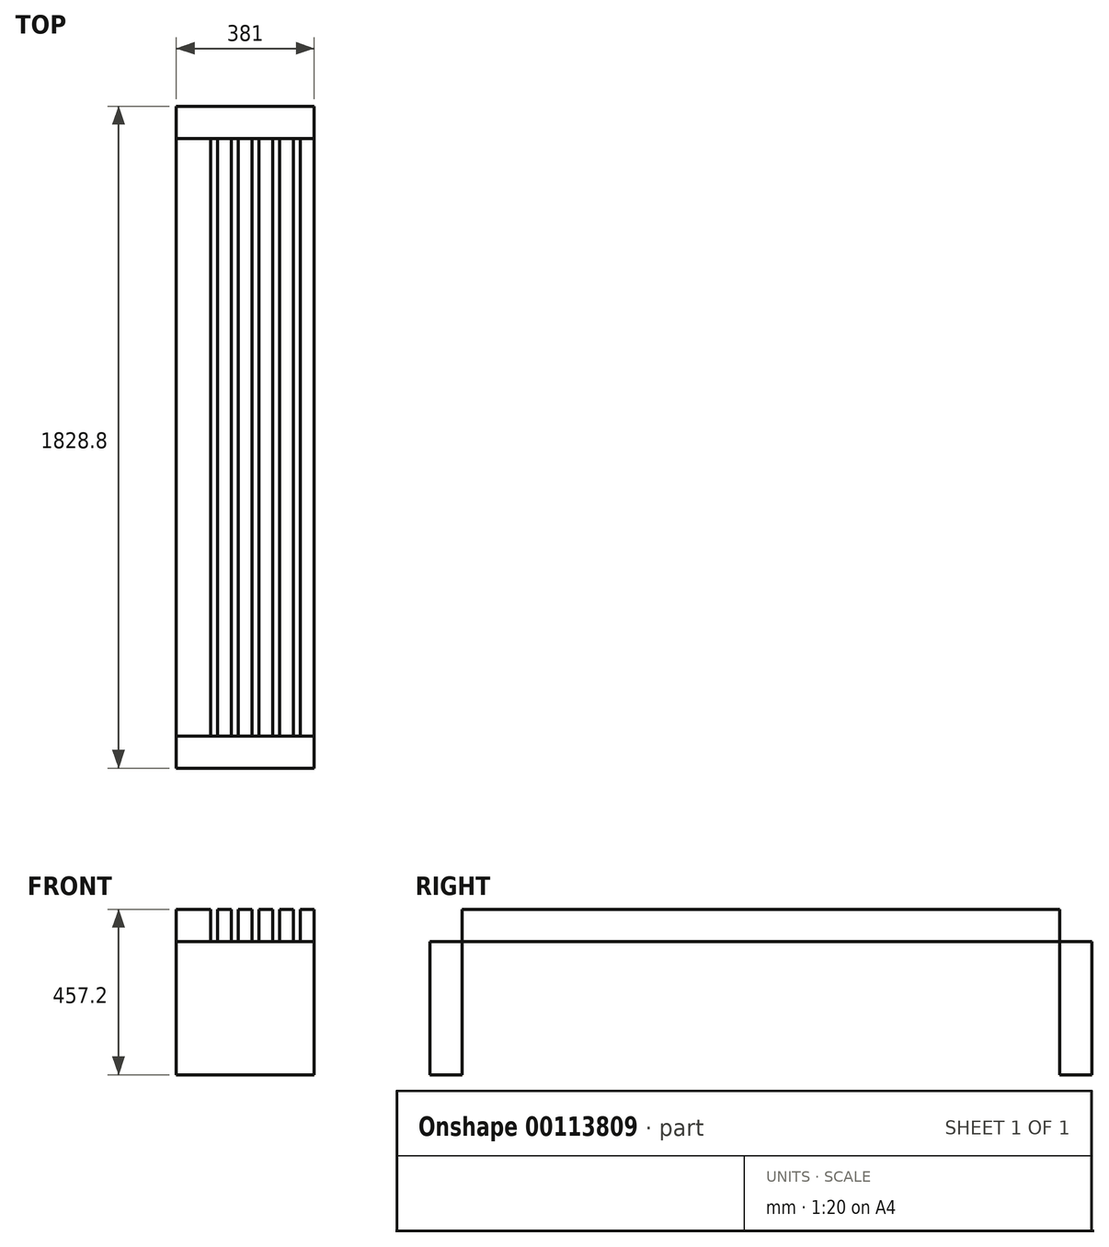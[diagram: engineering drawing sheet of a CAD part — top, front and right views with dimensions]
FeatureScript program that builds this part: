
annotation { "Feature Type Name" : "Feature", "Feature Type Description" : "" }
export const myFeature = defineFeature(function(context is Context, id is Id, definition is map)
    precondition{}
    {
        {
            var Q0;
            Q0=qCreatedBy(makeId("Right.planeOp"),FACE);
            var sketch = newSketch(context, id + "F0", { "sketchPlane" : qUnion([Q0])});
            skLineSegment(sketch, "E0.bottom", {"start": v(-914.4, 0) * mm, "end": v(-825.5, 0) * mm});
            skLineSegment(sketch, "E0.top", {"start": v(-914.4, 457.2) * mm, "end": v(-825.5, 457.2) * mm});
            skLineSegment(sketch, "E0.left", {"start": v(-914.4, 0) * mm, "end": v(-914.4, 457.2) * mm});
            skLineSegment(sketch, "E0.right", {"start": v(-825.5, 0) * mm, "end": v(-825.5, 457.2) * mm});
            skLineSegment(sketch, "E1.bottom", {"start": v(-914.4, 457.2) * mm, "end": v(914.4, 457.2) * mm});
            skLineSegment(sketch, "E1.top", {"start": v(-914.4, 368.3) * mm, "end": v(914.4, 368.3) * mm});
            skLineSegment(sketch, "E1.left", {"start": v(-914.4, 457.2) * mm, "end": v(-914.4, 368.3) * mm});
            skLineSegment(sketch, "E1.right", {"start": v(914.4, 457.2) * mm, "end": v(914.4, 368.3) * mm});
            skLineSegment(sketch, "E2.bottom", {"start": v(914.4, 457.2) * mm, "end": v(825.5, 457.2) * mm});
            skLineSegment(sketch, "E2.top", {"start": v(914.4, 0) * mm, "end": v(825.5, 0) * mm});
            skLineSegment(sketch, "E2.left", {"start": v(914.4, 457.2) * mm, "end": v(914.4, 0) * mm});
            skLineSegment(sketch, "E2.right", {"start": v(825.5, 457.2) * mm, "end": v(825.5, 0) * mm});
            skSolve(sketch);
        }
        {
            var Q0;
            {var subQ5=sQuery(id+"F0.wireOp",EDGE,"E1.left");Q0=makeQuery(id+"F0.imprint","IMPRINT",FACE,{"disambiguationData":[TD([[makeQuery(id+"F0.imprint","IMPRINT",EDGE,{"derivedFrom":subQ5}),1.0]])]});}
            var Q1;
            {var subQ0=sQuery(id+"F0.wireOp",EDGE,"E0.bottom");Q1=makeQuery(id+"F0.imprint","IMPRINT",FACE,{"disambiguationData":[TD([[makeQuery(id+"F0.imprint","IMPRINT",EDGE,{"derivedFrom":subQ0}),1.0]])]});}
            var Q2;
            {var subQ0=sQuery(id+"F0.wireOp",EDGE,"E1.bottom");var subQ1=sQuery(id+"F0.wireOp",EDGE,"E0.right");var subQ2=makeQuery(id+"F0.imprint","INTERSECT",VERTEX,{"derivedFrom":[subQ1,subQ0]});Q2=makeQuery(id+"F0.imprint","IMPRINT",FACE,{"disambiguationData":[TD([[makeQuery(id+"F0.imprint","IMPRINT",EDGE,{"disambiguationData":[TD([[subQ2,1.0]])],"derivedFrom":subQ1}),-1.0]])]});}
            var Q3;
            {var subQ5=sQuery(id+"F0.wireOp",EDGE,"E2.bottom");Q3=makeQuery(id+"F0.imprint","IMPRINT",FACE,{"disambiguationData":[TD([[makeQuery(id+"F0.imprint","IMPRINT",EDGE,{"derivedFrom":subQ5}),1.0]])]});}
            var Q4;
            {var subQ5=sQuery(id+"F0.wireOp",EDGE,"E2.top");Q4=makeQuery(id+"F0.imprint","IMPRINT",FACE,{"disambiguationData":[TD([[makeQuery(id+"F0.imprint","IMPRINT",EDGE,{"derivedFrom":subQ5}),-1.0]])]});}
            extrude(context, id + "F1", {"entities" : qUnion([Q0, Q1, Q2, Q3, Q4]), "depth" : 400.05 * mm - 19.05 * mm, "symmetric" : true});
        }
        {
            var Q0;
            Q0=makeQuery(id+"F1.opExtrude","SWEPT_FACE",FACE,{"disambiguationData":[OSD([sQuery(id+"F0.wireOp",EDGE,"E1.bottom"),sQuery(id+"F0.wireOp",EDGE,"E2.bottom")])]});
            var sketch = newSketch(context, id + "F2", { "sketchPlane" : qUnion([Q0])});
            skLineSegment(sketch, "E3.bottom", {"start": v(-152.4, 825.5) * mm, "end": v(-133.35, 825.5) * mm});
            skLineSegment(sketch, "E3.top", {"start": v(-152.4, -825.5) * mm, "end": v(-133.35, -825.5) * mm});
            skLineSegment(sketch, "E3.left", {"start": v(-152.4, 825.5) * mm, "end": v(-152.4, -825.5) * mm});
            skLineSegment(sketch, "E3.right", {"start": v(-133.35, 825.5) * mm, "end": v(-133.35, -825.5) * mm});
            skLineSegment(sketch, "E4.1.0.0", {"start": v(-95.25, 825.5) * mm, "end": v(-95.25, -825.5) * mm});
            skLineSegment(sketch, "E4.1.0.1", {"start": v(-76.2, 825.5) * mm, "end": v(-76.2, -825.5) * mm});
            skLineSegment(sketch, "E4.1.0.2", {"start": v(-95.25, 825.5) * mm, "end": v(-76.2, 825.5) * mm});
            skLineSegment(sketch, "E4.1.0.3", {"start": v(-95.25, -825.5) * mm, "end": v(-76.2, -825.5) * mm});
            skLineSegment(sketch, "E4.2.0.0", {"start": v(-38.1, 825.5) * mm, "end": v(-38.1, -825.5) * mm});
            skLineSegment(sketch, "E4.2.0.1", {"start": v(-19.05, 825.5) * mm, "end": v(-19.05, -825.5) * mm});
            skLineSegment(sketch, "E4.2.0.2", {"start": v(-38.1, 825.5) * mm, "end": v(-19.05, 825.5) * mm});
            skLineSegment(sketch, "E4.2.0.3", {"start": v(-38.1, -825.5) * mm, "end": v(-19.05, -825.5) * mm});
            skLineSegment(sketch, "E4.3.0.0", {"start": v(19.05, 825.5) * mm, "end": v(19.05, -825.5) * mm});
            skLineSegment(sketch, "E4.3.0.1", {"start": v(38.1, 825.5) * mm, "end": v(38.1, -825.5) * mm});
            skLineSegment(sketch, "E4.3.0.2", {"start": v(19.05, 825.5) * mm, "end": v(38.1, 825.5) * mm});
            skLineSegment(sketch, "E4.3.0.3", {"start": v(19.05, -825.5) * mm, "end": v(38.1, -825.5) * mm});
            skLineSegment(sketch, "E4.4.0.0", {"start": v(76.2, 825.5) * mm, "end": v(76.2, -825.5) * mm});
            skLineSegment(sketch, "E4.4.0.1", {"start": v(95.25, 825.5) * mm, "end": v(95.25, -825.5) * mm});
            skLineSegment(sketch, "E4.4.0.2", {"start": v(76.2, 825.5) * mm, "end": v(95.25, 825.5) * mm});
            skLineSegment(sketch, "E4.4.0.3", {"start": v(76.2, -825.5) * mm, "end": v(95.25, -825.5) * mm});
            skLineSegment(sketch, "E4.5.0.0", {"start": v(133.35, 825.5) * mm, "end": v(133.35, -825.5) * mm});
            skLineSegment(sketch, "E4.5.0.1", {"start": v(152.4, 825.5) * mm, "end": v(152.4, -825.5) * mm});
            skLineSegment(sketch, "E4.5.0.2", {"start": v(133.35, 825.5) * mm, "end": v(152.4, 825.5) * mm});
            skLineSegment(sketch, "E4.5.0.3", {"start": v(133.35, -825.5) * mm, "end": v(152.4, -825.5) * mm});
            skLineSegment(sketch, "E4.direction1", {"start": v(-152.4, -825.5) * mm, "end": v(-95.25, -825.5) * mm, "construction": true});
            skSolve(sketch);
        }
        {
            var Q0;
            Q0=makeQuery(id+"F2.imprint","IMPRINT",FACE,{"disambiguationData":[TD([[makeQuery(id+"F2.imprint","IMPRINT",EDGE,{"derivedFrom":sQuery(id+"F2.wireOp",EDGE,"E4.1.0.0")}),1.0]])]});
            var Q1;
            Q1=makeQuery(id+"F2.imprint","IMPRINT",FACE,{"disambiguationData":[TD([[makeQuery(id+"F2.imprint","IMPRINT",EDGE,{"derivedFrom":sQuery(id+"F2.wireOp",EDGE,"E4.2.0.0")}),1.0]])]});
            var Q2;
            Q2=makeQuery(id+"F2.imprint","IMPRINT",FACE,{"disambiguationData":[TD([[makeQuery(id+"F2.imprint","IMPRINT",EDGE,{"derivedFrom":sQuery(id+"F2.wireOp",EDGE,"E4.3.0.0")}),1.0]])]});
            var Q3;
            Q3=makeQuery(id+"F2.imprint","IMPRINT",FACE,{"disambiguationData":[TD([[makeQuery(id+"F2.imprint","IMPRINT",EDGE,{"derivedFrom":sQuery(id+"F2.wireOp",EDGE,"E4.4.0.0")}),1.0]])]});
            var Q4;
            Q4=makeQuery(id+"F2.imprint","IMPRINT",FACE,{"disambiguationData":[TD([[makeQuery(id+"F2.imprint","IMPRINT",EDGE,{"derivedFrom":sQuery(id+"F2.wireOp",EDGE,"E4.5.0.0")}),1.0]])]});
            var Q5;
            Q5=makeQuery(id+"F2.imprint","IMPRINT",FACE,{"disambiguationData":[TD([[makeQuery(id+"F2.imprint","IMPRINT",EDGE,{"derivedFrom":sQuery(id+"F2.wireOp",EDGE,"E3.bottom")}),-1.0]])]});
            extrude(context, id + "F3", {"entities" : qUnion([Q0, Q1, Q2, Q3, Q4, Q5]), "operationType" : NewBodyOperationType.REMOVE, "oppositeDirection" : true, "depth" : 101.6 * mm});
        }
    });
